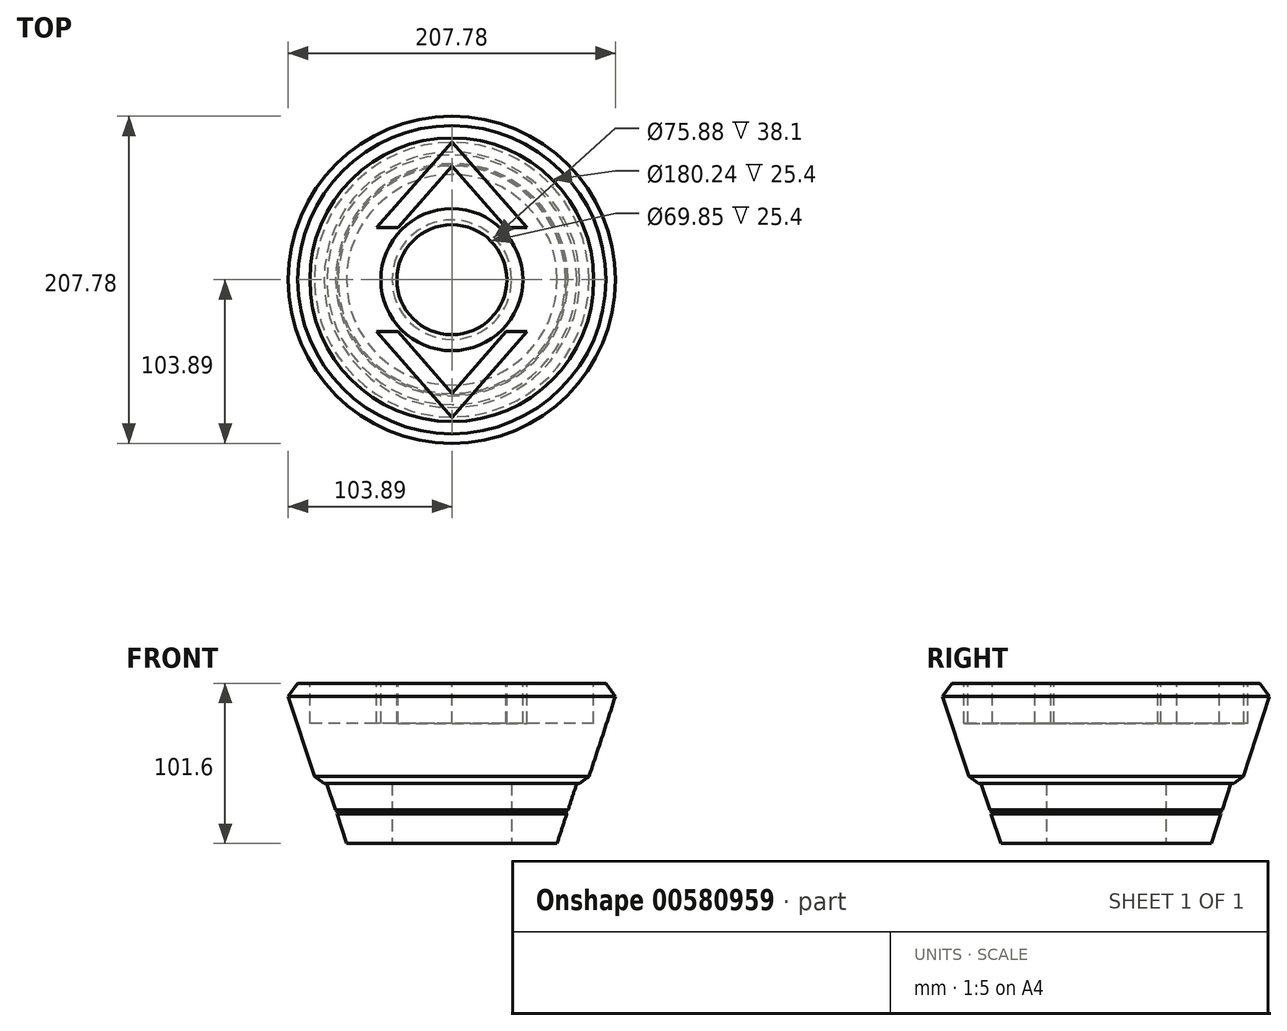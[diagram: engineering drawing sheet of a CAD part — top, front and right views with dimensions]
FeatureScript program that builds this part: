
annotation { "Feature Type Name" : "Feature", "Feature Type Description" : "" }
export const myFeature = defineFeature(function(context is Context, id is Id, definition is map)
    precondition{}
    {
        {
            var Q0;
            Q0=qCreatedBy(makeId("Top.planeOp"),FACE);
            var sketch = newSketch(context, id + "F0", { "sketchPlane" : qUnion([Q0])});
            skCircle(sketch, "E0", {"center": v(0, 0) * mm, "radius": 66.85 * mm});
            skSolve(sketch);
        }
        {
            var Q0;
            Q0=qCreatedBy(makeId("Top.planeOp"),FACE);
            cPlane(context, id + "F1", {"entities" : qUnion([Q0]), "cplaneType" : CPlaneType.OFFSET, "offset" : 101.6 * mm, "width" : 152.4 * mm, "height" : 152.4 * mm});
        }
        {
            var Q0;
            Q0=qCreatedBy(id+"F1.planeOp",FACE);
            var sketch = newSketch(context, id + "F2", { "sketchPlane" : qUnion([Q0])});
            skCircle(sketch, "E1", {"center": v(0, 0) * mm, "radius": 100.28 * mm});
            skSolve(sketch);
        }
        {
            var Q0;
            Q0=makeQuery(id+"F2.imprint","IMPRINT",FACE,{"disambiguationData":[TD([[makeQuery(id+"F2.imprint","IMPRINT",EDGE,{"derivedFrom":sQuery(id+"F2.wireOp",EDGE,"E1")}),1.0]])]});
            var Q1;
            Q1=makeQuery(id+"F0.imprint","IMPRINT",FACE,{"disambiguationData":[TD([[makeQuery(id+"F0.imprint","IMPRINT",EDGE,{"derivedFrom":sQuery(id+"F0.wireOp",EDGE,"E0")}),1.0]])]});
            var Q2;
            Q2=sQuery(id+"F2.wireOp",EDGE,"Eyu8YDiN-lEGU-Wuxt-0ncA-RZLAWeJK4OgB");
            var Q3;
            Q3=sQuery(id+"F0.wireOp",EDGE,"fgfE4CqQ-t5n6-ucAx-yhIW-5wF2yx0Jya2k");
            loft(context, id + "F3", {"sheetProfilesArray" : [{ "sheetProfileEntities" : qUnion([Q0]) }, { "sheetProfileEntities" : qUnion([Q1]) }], "wireProfilesArray" : [{ "wireProfileEntities" : qUnion([Q2]) }, { "wireProfileEntities" : qUnion([Q3]) }]});
        }
        {
            var Q0;
            Q0=qCreatedBy(makeId("Top.planeOp"),FACE);
            var sketch = newSketch(context, id + "F4", { "sketchPlane" : qUnion([Q0])});
            skCircle(sketch, "E2", {"center": v(0, 0) * mm, "radius": 37.94 * mm});
            skSolve(sketch);
        }
        {
            var Q0;
            Q0=makeQuery(id+"F4.imprint","IMPRINT",FACE,{"disambiguationData":[TD([[makeQuery(id+"F4.imprint","IMPRINT",EDGE,{"derivedFrom":sQuery(id+"F4.wireOp",EDGE,"E2")}),1.0]])]});
            extrude(context, id + "F5", {"entities" : qUnion([Q0]), "operationType" : NewBodyOperationType.REMOVE, "depth" : 53.34 * mm, "offsetDistance" : 25.4 * mm});
        }
        {
            var Q0;
            Q0=qCreatedBy(makeId("Top.planeOp"),FACE);
            cPlane(context, id + "F6", {"entities" : qUnion([Q0]), "cplaneType" : CPlaneType.OFFSET, "offset" : 38.1 * mm, "width" : 152.4 * mm, "height" : 152.4 * mm});
        }
        {
            var Q0;
            Q0=qCreatedBy(id+"F6.planeOp",FACE);
            var sketch = newSketch(context, id + "F7", { "sketchPlane" : qUnion([Q0])});
            skCircle(sketch, "E3", {"center": v(0, 0) * mm, "radius": 85.73 * mm});
            skSolve(sketch);
        }
        {
            var Q0;
            Q0=qCreatedBy(id+"F1.planeOp",FACE);
            var sketch = newSketch(context, id + "F8", { "sketchPlane" : qUnion([Q0])});
            skCircle(sketch, "E4", {"center": v(0, 0) * mm, "radius": 106.63 * mm});
            skSolve(sketch);
        }
        {
            var Q1;
            Q1=makeQuery(id+"F7.imprint","IMPRINT",FACE,{"disambiguationData":[TD([[makeQuery(id+"F7.imprint","IMPRINT",EDGE,{"derivedFrom":sQuery(id+"F7.wireOp",EDGE,"E3")}),1.0]])]});
            var Q2;
            Q2=makeQuery(id+"F8.imprint","IMPRINT",FACE,{"disambiguationData":[TD([[makeQuery(id+"F8.imprint","IMPRINT",EDGE,{"derivedFrom":sQuery(id+"F8.wireOp",EDGE,"E4")}),1.0]])]});
            loft(context, id + "F9", {"operationType" : NewBodyOperationType.ADD, "sheetProfilesArray" : [{ "sheetProfileEntities" : qUnion([Q1]) }, { "sheetProfileEntities" : qUnion([Q2]) }]});
        }
        {
            var Q0;
            Q0=makeQuery(id+"F9.opLoft","MID_CAP_EDGE",EDGE,{"disambiguationData":[OSD([sQuery(id+"F7.wireOp",EDGE,"E3")])],"capPos":0.0});
            chamfer(context, id + "F10", {"entities" : qUnion([Q0]), "width" : 6.35 * mm, "tangentPropagation" : true});
        }
        {
            var Q0;
            Q0=makeQuery(id+"F9.opLoft","MID_CAP_EDGE",EDGE,{"disambiguationData":[OSD([sQuery(id+"F7.wireOp",EDGE,"E3"),sQuery(id+"F8.wireOp",EDGE,"E4")])],"capPos":1.0});
            chamfer(context, id + "F11", {"entities" : qUnion([Q0]), "width" : 6.35 * mm, "tangentPropagation" : true});
        }
        {
            var Q0;
            Q0=qCreatedBy(makeId("Front.planeOp"),FACE);
            var sketch = newSketch(context, id + "F12", { "sketchPlane" : qUnion([Q0])});
            skLineSegment(sketch, "E5", {"start": v(-79.4, 38.11) * mm, "end": v(-66.85, 0) * mm});
            skLineSegment(sketch, "E6", {"start": v(-73.8, 21.14) * mm, "end": v(-72.2, 20.33) * mm});
            skLineSegment(sketch, "E7", {"start": v(-72.2, 20.33) * mm, "end": v(-73.02, 18.73) * mm});
            skSolve(sketch);
        }
        {
            var Q0;
            Q0=qCreatedBy(makeId("Right.planeOp"),FACE);
            var sketch = newSketch(context, id + "F13", { "sketchPlane" : qUnion([Q0])});
            skLineSegment(sketch, "E8", {"start": v(0, 0) * mm, "end": v(0, 184.2) * mm});
            skSolve(sketch);
        }
        {
            var Q0;
            Q0=qSketchRegion(id+"F12",true);
            var Q1;
            Q1=sQuery(id+"F13.wireOp",EDGE,"E8");
            revolve(context, id + "F14", {"operationType" : NewBodyOperationType.REMOVE, "entities" : qUnion([Q0]), "axis" : qUnion([Q1]), "revolveType" : RevolveType.FULL, "oppositeDirection" : true});
        }
        {
            var Q0;
            Q0=makeQuery(id+"F9.boolean.opBoolean","MERGE",FACE,{"derivedFrom":[makeQuery(id+"F3.opLoft","CAP_FACE",FACE,{"disambiguationData":[OSD([makeQuery(id+"F2.imprint","IMPRINT",FACE,{"disambiguationData":[TD([[makeQuery(id+"F2.imprint","IMPRINT",EDGE,{"derivedFrom":sQuery(id+"F2.wireOp",EDGE,"E1")}),1.0]])]})])],"isStart":true}),makeQuery(id+"F9.opLoft","CAP_FACE",FACE,{"disambiguationData":[OSD([makeQuery(id+"F8.imprint","IMPRINT",FACE,{"disambiguationData":[TD([[makeQuery(id+"F8.imprint","IMPRINT",EDGE,{"derivedFrom":sQuery(id+"F8.wireOp",EDGE,"E4")}),1.0]])]})])],"isStart":true})]});
            var sketch = newSketch(context, id + "F15", { "sketchPlane" : qUnion([Q0])});
            skCircle(sketch, "E9", {"center": v(0, 0) * mm, "radius": 100.28 * mm});
            skCircle(sketch, "E10.0", {"center": v(0, 0) * mm, "radius": 90.12 * mm});
            skCircle(sketch, "E11.0", {"center": v(0, 0) * mm, "radius": 34.93 * mm});
            skCircle(sketch, "E12", {"center": v(0, 0) * mm, "radius": 45.09 * mm});
            skLineSegment(sketch, "E13", {"start": v(0, 87.58) * mm, "end": v(-47.8, 33.02) * mm});
            skLineSegment(sketch, "E14", {"start": v(0, 0) * mm, "end": v(0, 15.87) * mm});
            skLineSegment(sketch, "E15", {"start": v(-34.29, 33.02) * mm, "end": v(0, 72.16) * mm});
            skLineSegment(sketch, "E16", {"start": v(-34.3, 33.02) * mm, "end": v(-47.8, 33.02) * mm});
            skLineSegment(sketch, "E17", {"start": v(0, 0) * mm, "end": v(13.2, 0) * mm});
            skLineSegment(sketch, "E18.MirrorCS", {"start": v(34.3, 33.02) * mm, "end": v(0, 72.16) * mm});
            skLineSegment(sketch, "E19.MirrorCS", {"start": v(0, 87.58) * mm, "end": v(47.8, 33.02) * mm});
            skLineSegment(sketch, "E20.MirrorCS", {"start": v(34.3, 33.02) * mm, "end": v(47.8, 33.02) * mm});
            skLineSegment(sketch, "E21.MirrorCS", {"start": v(-34.3, -33.02) * mm, "end": v(0, -72.16) * mm});
            skLineSegment(sketch, "E22.MirrorCS", {"start": v(-34.3, -33.02) * mm, "end": v(-47.8, -33.02) * mm});
            skLineSegment(sketch, "E23.MirrorCS", {"start": v(0, -87.58) * mm, "end": v(-47.8, -33.02) * mm});
            skLineSegment(sketch, "E24.MirrorCS", {"start": v(0, -87.58) * mm, "end": v(47.8, -33.02) * mm});
            skLineSegment(sketch, "E25.MirrorCS", {"start": v(34.3, -33.02) * mm, "end": v(0, -72.16) * mm});
            skLineSegment(sketch, "E26.MirrorCS", {"start": v(34.3, -33.02) * mm, "end": v(47.8, -33.02) * mm});
            skSolve(sketch);
        }
        {
            var Q0;
            {var subQ0=sQuery(id+"F15.wireOp",EDGE,"E18.MirrorCS");var subQ1=sQuery(id+"F15.wireOp",EDGE,"E12");var subQ2=makeQuery(id+"F15.imprint","INTERSECT",VERTEX,{"derivedFrom":[subQ1,subQ0]});Q0=makeQuery(id+"F15.imprint","IMPRINT",FACE,{"disambiguationData":[TD([[makeQuery(id+"F15.imprint","IMPRINT",EDGE,{"disambiguationData":[TD([[subQ2,-1.0]])],"derivedFrom":subQ1}),-1.0]])]});}
            var Q1;
            Q1=makeQuery(id+"F15.imprint","IMPRINT",FACE,{"disambiguationData":[TD([[makeQuery(id+"F15.imprint","IMPRINT",EDGE,{"derivedFrom":sQuery(id+"F15.wireOp",EDGE,"E10.0")}),1.0]])]});
            var Q2;
            Q2=makeQuery(id+"F15.imprint","IMPRINT",FACE,{"disambiguationData":[TD([[makeQuery(id+"F15.imprint","IMPRINT",EDGE,{"derivedFrom":sQuery(id+"F15.wireOp",EDGE,"E11.0")}),1.0]])]});
            var Q3;
            {var subQ0=sQuery(id+"F15.wireOp",EDGE,"E21.MirrorCS");var subQ1=sQuery(id+"F15.wireOp",EDGE,"E12");var subQ2=makeQuery(id+"F15.imprint","INTERSECT",VERTEX,{"derivedFrom":[subQ1,subQ0]});Q3=makeQuery(id+"F15.imprint","IMPRINT",FACE,{"disambiguationData":[TD([[makeQuery(id+"F15.imprint","IMPRINT",EDGE,{"disambiguationData":[TD([[subQ2,-1.0]])],"derivedFrom":subQ1}),-1.0]])]});}
            extrude(context, id + "F16", {"entities" : qUnion([Q0, Q1, Q2, Q3]), "operationType" : NewBodyOperationType.REMOVE, "oppositeDirection" : true, "depth" : 25.4 * mm, "offsetDistance" : 25.4 * mm});
        }
    });
